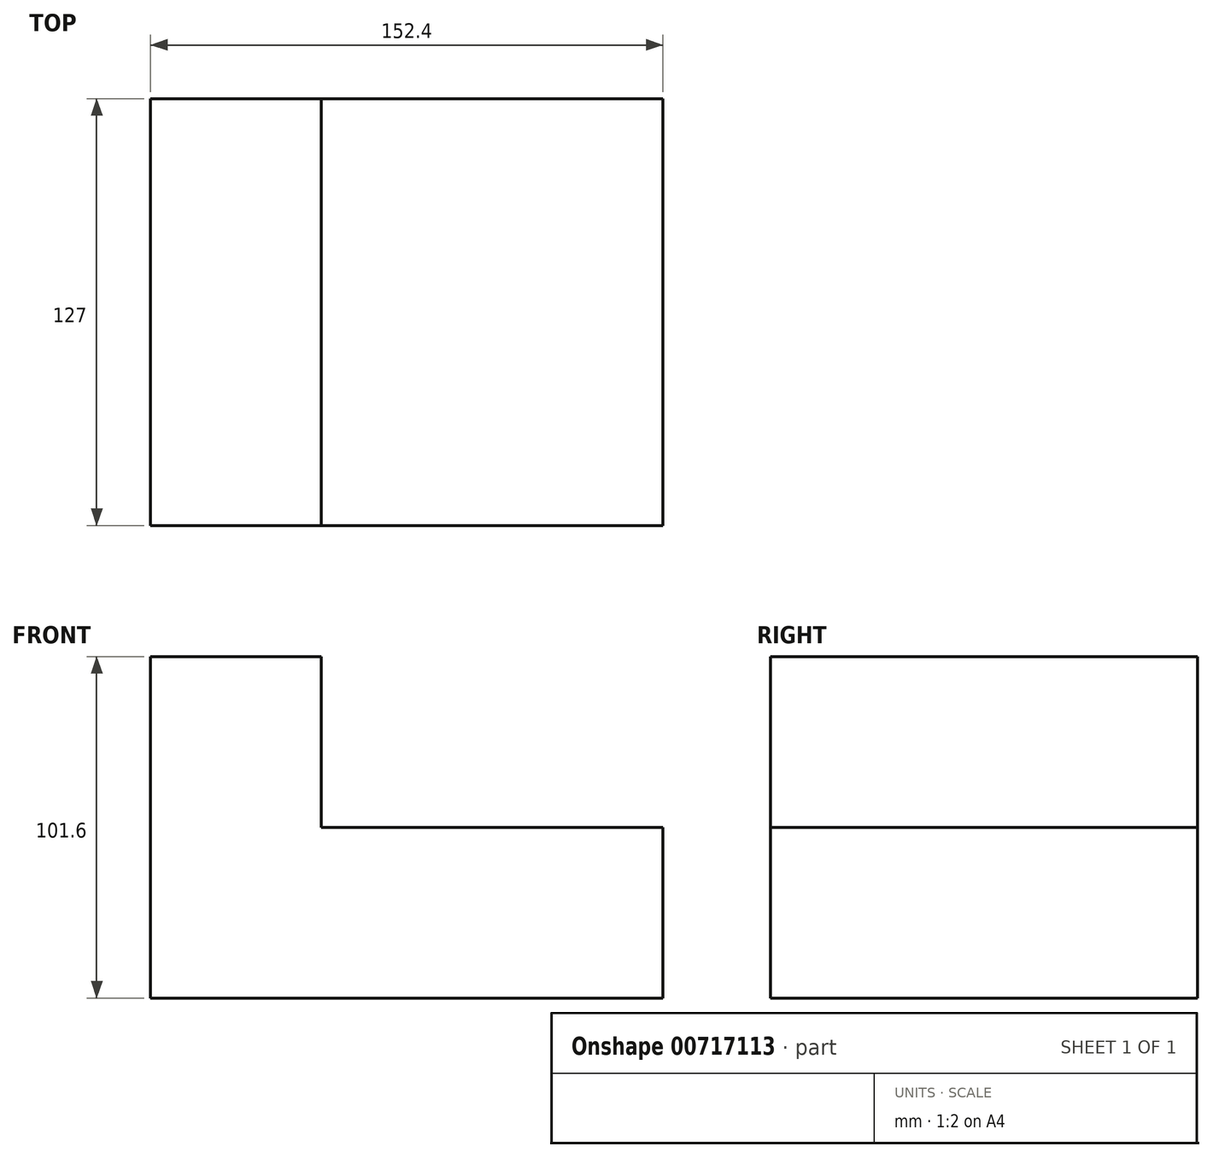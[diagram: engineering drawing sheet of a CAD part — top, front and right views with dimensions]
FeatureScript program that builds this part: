
annotation { "Feature Type Name" : "Feature", "Feature Type Description" : "" }
export const myFeature = defineFeature(function(context is Context, id is Id, definition is map)
    precondition{}
    {
        {
            var Q0;
            Q0=qCreatedBy(makeId("Front.planeOp"),FACE);
            var sketch = newSketch(context, id + "F0", { "sketchPlane" : qUnion([Q0])});
            skLineSegment(sketch, "E0", {"start": v(-73.73, 0) * mm, "end": v(78.67, 0) * mm});
            skLineSegment(sketch, "E1", {"start": v(78.67, 0) * mm, "end": v(78.67, 50.8) * mm});
            skLineSegment(sketch, "E2", {"start": v(78.67, 50.8) * mm, "end": v(-22.93, 50.8) * mm});
            skLineSegment(sketch, "E3", {"start": v(-22.93, 50.8) * mm, "end": v(-22.93, 101.6) * mm});
            skLineSegment(sketch, "E4", {"start": v(-22.93, 101.6) * mm, "end": v(-73.73, 101.6) * mm});
            skLineSegment(sketch, "E5", {"start": v(-73.73, 101.6) * mm, "end": v(-73.73, 0) * mm});
            skSolve(sketch);
        }
        {
            var Q0;
            Q0=makeQuery(id+"F0.imprint","IMPRINT",FACE,{"disambiguationData":[TD([[makeQuery(id+"F0.imprint","IMPRINT",EDGE,{"derivedFrom":sQuery(id+"F0.wireOp",EDGE,"E0")}),1.0]])]});
            extrude(context, id + "F1", {"entities" : qUnion([Q0]), "depth" : 127 * mm, "offsetDistance" : 25.4 * mm});
        }
    });
